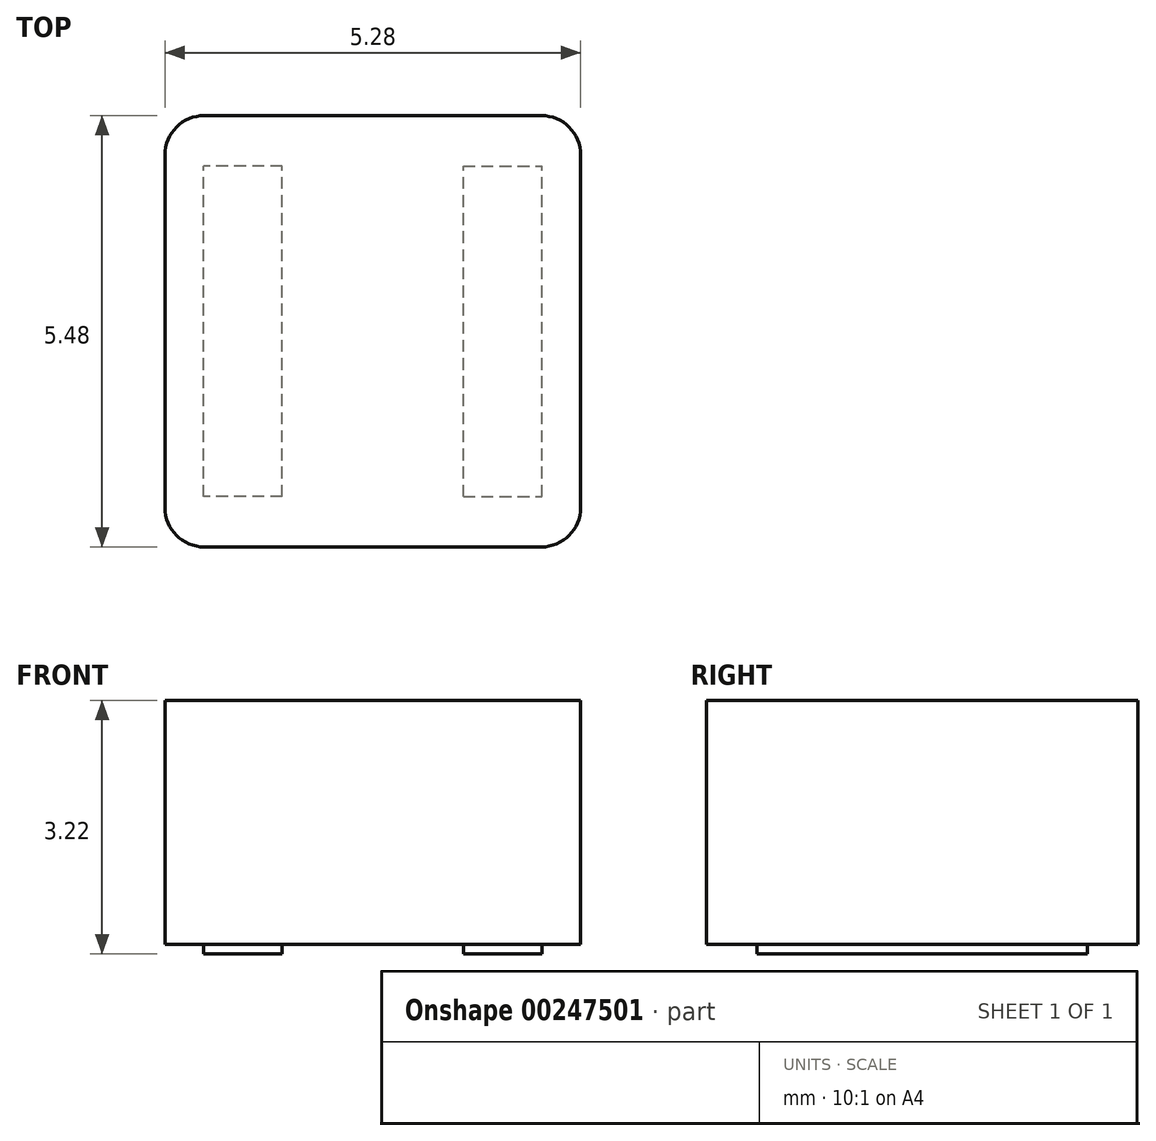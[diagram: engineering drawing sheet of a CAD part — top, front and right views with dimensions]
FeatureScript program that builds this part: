
annotation { "Feature Type Name" : "Feature", "Feature Type Description" : "" }
export const myFeature = defineFeature(function(context is Context, id is Id, definition is map)
    precondition{}
    {
        {
            var Q0;
            Q0=qCreatedBy(makeId("Top.planeOp"),FACE);
            var sketch = newSketch(context, id + "F0", { "sketchPlane" : qUnion([Q0])});
            skLineSegment(sketch, "E0.bottom", {"start": v(2.64, -2.74) * mm, "end": v(-2.64, -2.74) * mm});
            skLineSegment(sketch, "E0.top", {"start": v(2.64, 2.74) * mm, "end": v(-2.64, 2.74) * mm});
            skLineSegment(sketch, "E0.left", {"start": v(2.64, -2.74) * mm, "end": v(2.64, 2.74) * mm});
            skLineSegment(sketch, "E0.right", {"start": v(-2.64, -2.74) * mm, "end": v(-2.64, 2.74) * mm});
            skPoint(sketch, "E0.middle", {"position": v(0, 0) * mm});
            skSolve(sketch);
        }
        {
            var Q0;
            Q0=qSketchRegion(id+"F0",true);
            extrude(context, id + "F1", {"entities" : qUnion([Q0]), "depth" : 3.1 * mm});
        }
        {
            var Q0;
            Q0=makeQuery(id+"F1.opExtrude","SWEPT_EDGE",EDGE,{"disambiguationData":[OSD([sQuery(id+"F0.wireOp",EDGE,"E0.bottom"),sQuery(id+"F0.wireOp",EDGE,"E0.right")])]});
            var Q1;
            Q1=makeQuery(id+"F1.opExtrude","SWEPT_EDGE",EDGE,{"disambiguationData":[OSD([sQuery(id+"F0.wireOp",EDGE,"E0.bottom"),sQuery(id+"F0.wireOp",EDGE,"E0.left")])]});
            var Q2;
            Q2=makeQuery(id+"F1.opExtrude","SWEPT_EDGE",EDGE,{"disambiguationData":[OSD([sQuery(id+"F0.wireOp",EDGE,"E0.top"),sQuery(id+"F0.wireOp",EDGE,"E0.left")])]});
            var Q3;
            Q3=makeQuery(id+"F1.opExtrude","SWEPT_EDGE",EDGE,{"disambiguationData":[OSD([sQuery(id+"F0.wireOp",EDGE,"E0.top"),sQuery(id+"F0.wireOp",EDGE,"E0.right")])]});
            fillet(context, id + "F2", {"entities" : qUnion([Q0, Q1, Q2, Q3]), "radius" : .5 * mm, "tangentPropagation" : true, "allowEdgeOverflow" : false});
        }
        {
            var Q0;
            Q0=makeQuery(id+"F1.opExtrude","CAP_FACE",FACE,{"disambiguationData":[OSD([sQuery(id+"F0.wireOp",EDGE,"E0.bottom"),sQuery(id+"F0.wireOp",EDGE,"E0.top"),sQuery(id+"F0.wireOp",EDGE,"E0.left"),sQuery(id+"F0.wireOp",EDGE,"E0.right")])],"isStart":true});
            var sketch = newSketch(context, id + "F3", { "sketchPlane" : qUnion([Q0])});
            skLineSegment(sketch, "E1", {"start": v(0, 3.33) * mm, "end": v(0, -3.7) * mm, "construction": true});
            skPoint(sketch, "E1.endSnap0", {"position": v(0, 2.74) * mm});
            skLineSegment(sketch, "E2", {"start": v(-4.12, 0) * mm, "end": v(4.38, 0) * mm, "construction": true});
            skLineSegment(sketch, "E3.bottom", {"start": v(1.15, 2.1) * mm, "end": v(2.15, 2.1) * mm});
            skLineSegment(sketch, "E3.top", {"start": v(1.15, -2.1) * mm, "end": v(2.15, -2.1) * mm});
            skLineSegment(sketch, "E3.left", {"start": v(1.15, 2.1) * mm, "end": v(1.15, -2.1) * mm});
            skLineSegment(sketch, "E3.right", {"start": v(2.15, 2.1) * mm, "end": v(2.15, -2.1) * mm});
            skPoint(sketch, "E3.middle", {"position": v(1.65, 0) * mm});
            skPoint(sketch, "E4.MirrorP", {"position": v(-1.65, 0) * mm});
            skLineSegment(sketch, "E5.MirrorCS", {"start": v(-2.15, 2.1) * mm, "end": v(-2.15, -2.1) * mm});
            skLineSegment(sketch, "E6.MirrorCS", {"start": v(-1.15, 2.1) * mm, "end": v(-1.15, -2.1) * mm});
            skLineSegment(sketch, "E7.MirrorCS", {"start": v(-1.15, 2.1) * mm, "end": v(-2.15, 2.1) * mm});
            skLineSegment(sketch, "E8.MirrorCS", {"start": v(-1.15, -2.1) * mm, "end": v(-2.15, -2.1) * mm});
            skSolve(sketch);
        }
        {
            var Q0;
            Q0=qSketchRegion(id+"F3",true);
            extrude(context, id + "F4", {"entities" : qUnion([Q0]), "depth" : .12 * mm});
        }
    });
